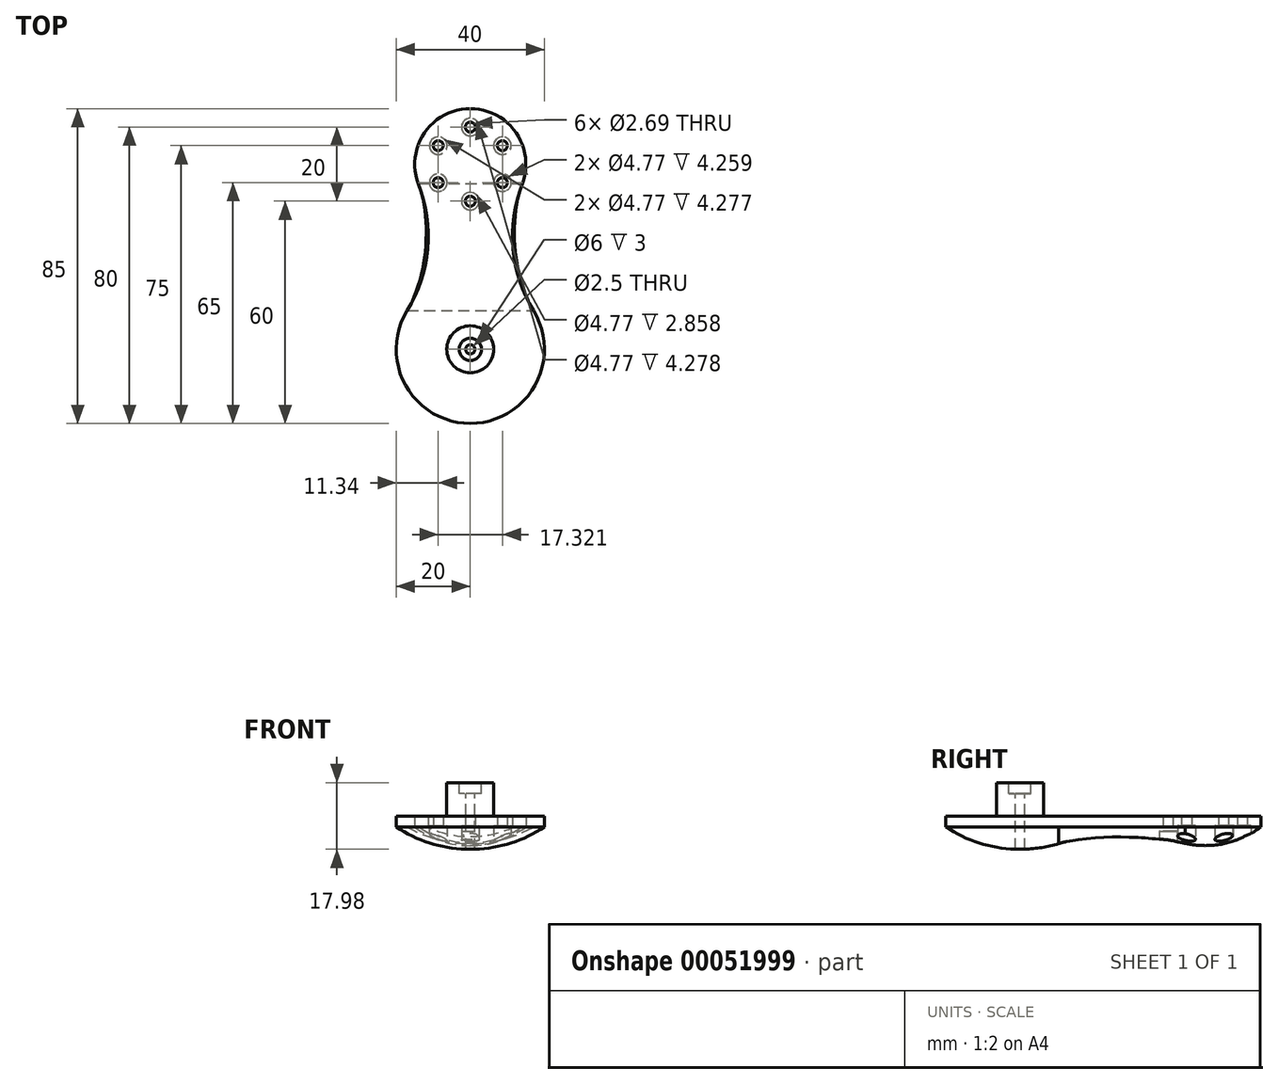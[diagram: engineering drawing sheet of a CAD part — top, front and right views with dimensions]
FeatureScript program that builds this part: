
annotation { "Feature Type Name" : "Feature", "Feature Type Description" : "" }
export const myFeature = defineFeature(function(context is Context, id is Id, definition is map)
    precondition{}
    {
        {
            var Q0;
            Q0=qCreatedBy(makeId("Top.planeOp"),FACE);
            var sketch = newSketch(context, id + "F0", { "sketchPlane" : qUnion([Q0])});
            skArc(sketch, "E0", {"start": v(-17.06, 10.44) * mm, "mid": v(0, -20) * mm, "end": v(17.06, 10.44) * mm});
            skArc(sketch, "E1", {"start": v(13.99, 44.58) * mm, "mid": v(0, 65) * mm, "end": v(-13.99, 44.58) * mm});
            skArc(sketch, "E2", {"start": v(-17.06, 10.44) * mm, "mid": v(-11.53, 27.15) * mm, "end": v(-13.99, 44.58) * mm});
            skArc(sketch, "E3", {"start": v(13.99, 44.58) * mm, "mid": v(11.53, 27.15) * mm, "end": v(17.06, 10.44) * mm});
            skSolve(sketch);
        }
        {
            var Q0;
            Q0 = qSketchRegion(id + "F0", true);
            extrude(context, id + "F1", {"entities" : qUnion([Q0]), "depth" : 3 * mm});
        }
        {
            var Q0;
            Q0=makeQuery(id+"F1.opExtrude","CAP_FACE",FACE,{"disambiguationData":[OSD([sQuery(id+"F0.wireOp",EDGE,"E0")])],"isStart":false});
            var sketch = newSketch(context, id + "F2", { "sketchPlane" : qUnion([Q0])});
            skCircle(sketch, "E4", {"center": v(0, 0) * mm, "radius": 6.35 * mm});
            skSolve(sketch);
        }
        {
            var Q0;
            Q0 = qSketchRegion(id + "F2", true);
            extrude(context, id + "F3", {"entities" : qUnion([Q0]), "operationType" : NewBodyOperationType.ADD, "depth" : 9 * mm});
        }
        {
            var Q0;
            Q0=makeQuery(id+"F3.opExtrude","CAP_FACE",FACE,{"disambiguationData":[OSD([sQuery(id+"F2.wireOp",EDGE,"E4")])],"isStart":false});
            var sketch = newSketch(context, id + "F4", { "sketchPlane" : qUnion([Q0])});
            skCircle(sketch, "E5", {"center": v(0, 0) * mm, "radius": 3 * mm});
            skSolve(sketch);
        }
        {
            var Q0;
            Q0 = qSketchRegion(id + "F4", true);
            extrude(context, id + "F5", {"entities" : qUnion([Q0]), "operationType" : NewBodyOperationType.REMOVE, "oppositeDirection" : true, "depth" : 3 * mm});
        }
        {
            var Q0;
            Q0=makeQuery(id+"F5.boolean.opBoolean","COPY",FACE,{"derivedFrom":makeQuery(id+"F5.opExtrude","CAP_FACE",FACE,{"disambiguationData":[OSD([sQuery(id+"F4.wireOp",EDGE,"E5")])],"isStart":false})});
            var sketch = newSketch(context, id + "F6", { "sketchPlane" : qUnion([Q0])});
            skCircle(sketch, "E6", {"center": v(0, 0) * mm, "radius": 1.25 * mm});
            skSolve(sketch);
        }
        {
            var Q0;
            Q0=qCreatedBy(makeId("Front.planeOp"),FACE);
            var sketch = newSketch(context, id + "F7", { "sketchPlane" : qUnion([Q0])});
            skLineSegment(sketch, "E7", {"start": v(0, 0) * mm, "end": v(0, -6) * mm});
            skLineSegment(sketch, "E8", {"start": v(0, 0) * mm, "end": v(-20, 0) * mm});
            skArc(sketch, "E9", {"start": v(-20, 0) * mm, "mid": v(-10.44, -4.47) * mm, "end": v(0, -6) * mm});
            skSolve(sketch);
        }
        {
            var Q0;
            Q0 = qSketchRegion(id + "F7", true);
            var Q1;
            Q1=sQuery(id+"F7.wireOp",EDGE,"E7");
            revolve(context, id + "F8", {"operationType" : NewBodyOperationType.ADD, "entities" : qUnion([Q0]), "axis" : qUnion([Q1]), "revolveType" : RevolveType.FULL, "oppositeDirection" : true});
        }
        {
            var Q0;
            Q0=qCreatedBy(makeId("Front.planeOp"),FACE);
            cPlane(context, id + "F9", {"entities" : qUnion([Q0]), "cplaneType" : CPlaneType.OFFSET, "offset" : 50 * mm, "oppositeDirection" : true, "width" : 150 * mm, "height" : 150 * mm});
        }
        {
            var Q0;
            Q0=qCreatedBy(id+"F9.planeOp",FACE);
            var sketch = newSketch(context, id + "F10", { "sketchPlane" : qUnion([Q0])});
            skLineSegment(sketch, "E10", {"start": v(0, 0) * mm, "end": v(0, -5) * mm});
            skLineSegment(sketch, "E11", {"start": v(0, 0) * mm, "end": v(15, 0) * mm});
            skArc(sketch, "E12", {"start": v(0, -5) * mm, "mid": v(7.9, -3.72) * mm, "end": v(15, 0) * mm});
            skSolve(sketch);
        }
        {
            var Q0;
            Q0 = qSketchRegion(id + "F10", true);
            var Q1;
            Q1=sQuery(id+"F10.wireOp",EDGE,"E10");
            revolve(context, id + "F11", {"operationType" : NewBodyOperationType.ADD, "entities" : qUnion([Q0]), "axis" : qUnion([Q1]), "revolveType" : RevolveType.FULL, "oppositeDirection" : true});
        }
        {
            var Q0;
            Q0=makeQuery(id+"F1.opExtrude","CAP_FACE",FACE,{"disambiguationData":[OSD([sQuery(id+"F0.wireOp",EDGE,"E0"),sQuery(id+"F0.wireOp",EDGE,"E1"),sQuery(id+"F0.wireOp",EDGE,"E2"),sQuery(id+"F0.wireOp",EDGE,"E3")])],"isStart":true});
            var sketch = newSketch(context, id + "F12", { "sketchPlane" : qUnion([Q0])});
            skLineSegment(sketch, "E13.bottom", {"start": v(-17.06, -10.44) * mm, "end": v(17.06, -10.44) * mm});
            skLineSegment(sketch, "E13.top", {"start": v(-17.06, -44.58) * mm, "end": v(17.06, -44.58) * mm});
            skLineSegment(sketch, "E13.left", {"start": v(-17.06, -10.44) * mm, "end": v(-17.06, -44.58) * mm});
            skLineSegment(sketch, "E13.right", {"start": v(17.06, -10.44) * mm, "end": v(17.06, -44.58) * mm});
            skSolve(sketch);
        }
        {
            var Q0;
            Q0 = qSketchRegion(id + "F12", true);
            extrude(context, id + "F13", {"entities" : qUnion([Q0]), "operationType" : NewBodyOperationType.REMOVE, "depth" : 25 * mm});
        }
        {
            var Q1;
            Q1=makeQuery(id+"F13.boolean.opBoolean","COPY",FACE,{"derivedFrom":makeQuery(id+"F13.opExtrude","SWEPT_FACE",FACE,{"disambiguationData":[OSD([sQuery(id+"F12.wireOp",EDGE,"E13.top")])]})});
            var Q2;
            Q2=makeQuery(id+"F13.boolean.opBoolean","COPY",FACE,{"derivedFrom":makeQuery(id+"F13.opExtrude","SWEPT_FACE",FACE,{"disambiguationData":[OSD([sQuery(id+"F12.wireOp",EDGE,"E13.bottom")])]})});
            loft(context, id + "F14", {"operationType" : NewBodyOperationType.ADD, "startCondition" : LoftEndDerivativeType.MATCH_TANGENT, "startMagnitude" : 1, "endCondition" : LoftEndDerivativeType.MATCH_TANGENT, "endMagnitude" : 1, "sheetProfilesArray" : [{ "sheetProfileEntities" : qUnion([Q1]) }, { "sheetProfileEntities" : qUnion([Q2]) }]});
        }
        {
            var Q0;
            Q0 = qSketchRegion(id + "F6", true);
            extrude(context, id + "F15", {"entities" : qUnion([Q0]), "operationType" : NewBodyOperationType.REMOVE, "endBound" : BoundingType.THROUGH_ALL, "oppositeDirection" : true, "depth" : 25 * mm});
        }
        {
            var Q0;
            Q0=qCreatedBy(makeId("Top.planeOp"),FACE);
            cPlane(context, id + "F16", {"entities" : qUnion([Q0]), "cplaneType" : CPlaneType.OFFSET, "offset" : 5 * mm, "oppositeDirection" : true, "width" : 150 * mm, "height" : 150 * mm});
        }
        {
            var Q0;
            Q0=qCreatedBy(id+"F16.planeOp",FACE);
            var sketch = newSketch(context, id + "F17", { "sketchPlane" : qUnion([Q0])});
            skPoint(sketch, "E14", {"position": v(0, 60) * mm});
            skPoint(sketch, "E15.1.0", {"position": v(-8.66, 55) * mm});
            skPoint(sketch, "E15.2.0", {"position": v(-8.66, 45) * mm});
            skPoint(sketch, "E15.center", {"position": v(0, 50) * mm});
            skPoint(sketch, "E16.0.3.0", {"position": v(0, 40) * mm});
            skPoint(sketch, "E16.0.4.0", {"position": v(8.66, 45) * mm});
            skPoint(sketch, "E16.0.5.0", {"position": v(8.66, 55) * mm});
            skSolve(sketch);
        }
        {
            var Q0;
            Q0=sQuery(id+"F17.wireOp",VERTEX,"E15.2.0");
            var Q1;
            Q1=sQuery(id+"F17.wireOp",VERTEX,"E16.0.3.0");
            var Q2;
            Q2=sQuery(id+"F17.wireOp",VERTEX,"E16.0.4.0");
            var Q3;
            Q3=sQuery(id+"F17.wireOp",VERTEX,"E16.0.5.0");
            var Q4;
            Q4=sQuery(id+"F17.wireOp",VERTEX,"E14");
            var Q5;
            Q5=sQuery(id+"F17.wireOp",VERTEX,"E15.1.0");
            var Q6;
            Q6=makeQuery(id+"F1.opExtrude","SWEPT_BODY",BODY,{"disambiguationData":[OSD([sQuery(id+"F0.wireOp",EDGE,"E0"),sQuery(id+"F0.wireOp",EDGE,"E1"),sQuery(id+"F0.wireOp",EDGE,"E2"),sQuery(id+"F0.wireOp",EDGE,"E3")])]});
            hole(context, id + "F18", {"style" : HoleStyle.C_BORE, "holeDiameter" : 2.69 * mm, "cBoreDiameter" : 4.77 * mm, "cBoreDepth" : 2.18 * mm, "endStyle" : HoleEndStyle.THROUGH, "oppositeDirection" : true, "locations" : qUnion([Q0, Q1, Q2, Q3, Q4, Q5]), "scope" : qUnion([Q6])});
        }
    });
